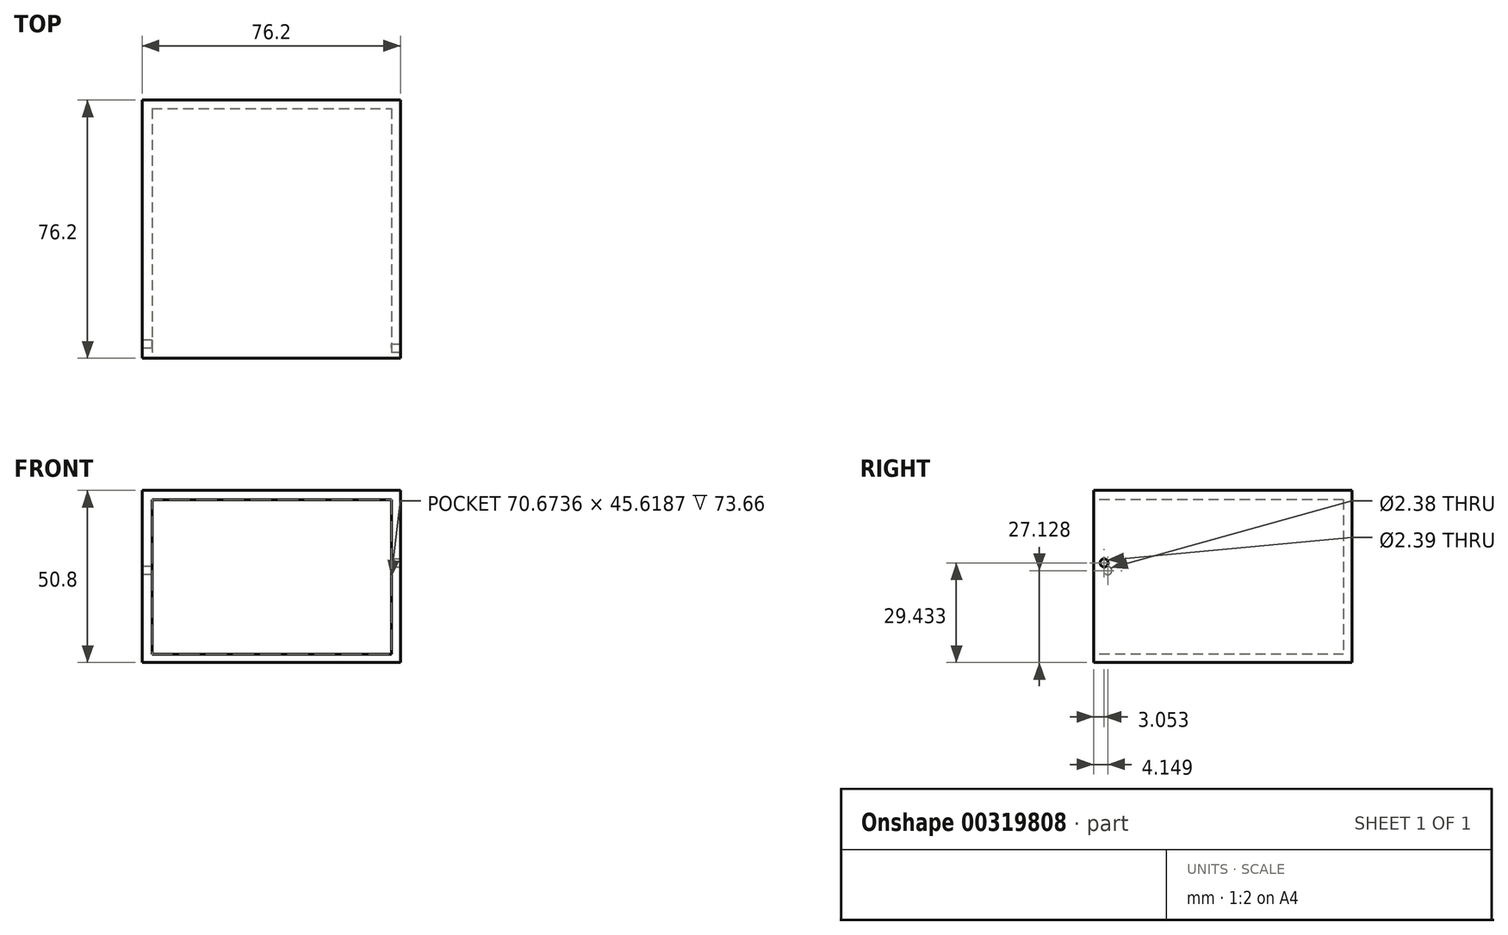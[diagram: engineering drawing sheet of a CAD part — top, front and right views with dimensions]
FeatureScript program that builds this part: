
annotation { "Feature Type Name" : "Feature", "Feature Type Description" : "" }
export const myFeature = defineFeature(function(context is Context, id is Id, definition is map)
    precondition{}
    {
        {
            var Q0;
            Q0=qCreatedBy(makeId("Front.planeOp"),FACE);
            var sketch = newSketch(context, id + "F0", { "sketchPlane" : qUnion([Q0])});
            skLineSegment(sketch, "E0.bottom", {"start": v(0, 0) * mm, "end": v(-76.2, 0) * mm});
            skLineSegment(sketch, "E0.top", {"start": v(0, 50.8) * mm, "end": v(-76.2, 50.8) * mm});
            skLineSegment(sketch, "E0.left", {"start": v(0, 0) * mm, "end": v(0, 50.8) * mm});
            skLineSegment(sketch, "E0.right", {"start": v(-76.2, 0) * mm, "end": v(-76.2, 50.8) * mm});
            skSolve(sketch);
        }
        {
            var Q0;
            Q0=makeQuery(id+"F0.imprint","IMPRINT",FACE,{"disambiguationData":[TD([[makeQuery(id+"F0.imprint","IMPRINT",EDGE,{"derivedFrom":sQuery(id+"F0.wireOp",EDGE,"E0.bottom")}),-1.0]])]});
            extrude(context, id + "F1", {"entities" : qUnion([Q0]), "depth" : 76.2 * mm});
        }
        {
            var Q0;
            Q0=makeQuery(id+"F1.opExtrude","CAP_FACE",FACE,{"disambiguationData":[OSD([sQuery(id+"F0.wireOp",EDGE,"E0.bottom"),sQuery(id+"F0.wireOp",EDGE,"E0.top"),sQuery(id+"F0.wireOp",EDGE,"E0.left"),sQuery(id+"F0.wireOp",EDGE,"E0.right")])],"isStart":false});
            var sketch = newSketch(context, id + "F2", { "sketchPlane" : qUnion([Q0])});
            skLineSegment(sketch, "E1.bottom", {"start": v(-73.27, 48.1) * mm, "end": v(-2.6, 48.1) * mm});
            skLineSegment(sketch, "E1.top", {"start": v(-73.27, 2.48) * mm, "end": v(-2.6, 2.48) * mm});
            skLineSegment(sketch, "E1.left", {"start": v(-73.27, 48.1) * mm, "end": v(-73.27, 2.48) * mm});
            skLineSegment(sketch, "E1.right", {"start": v(-2.6, 48.1) * mm, "end": v(-2.6, 2.48) * mm});
            skSolve(sketch);
        }
        {
            var Q0;
            Q0=makeQuery(id+"F2.imprint","IMPRINT",FACE,{"disambiguationData":[TD([[makeQuery(id+"F2.imprint","IMPRINT",EDGE,{"derivedFrom":sQuery(id+"F2.wireOp",EDGE,"E1.bottom")}),-1.0]])]});
            extrude(context, id + "F3", {"entities" : qUnion([Q0]), "operationType" : NewBodyOperationType.REMOVE, "oppositeDirection" : true, "depth" : 73.66 * mm});
        }
        {
            var Q0;
            Q0=makeQuery(id+"F1.opExtrude","SWEPT_FACE",FACE,{"disambiguationData":[OSD([sQuery(id+"F0.wireOp",EDGE,"E0.right")])]});
            var sketch = newSketch(context, id + "F4", { "sketchPlane" : qUnion([Q0])});
            skCircle(sketch, "E2", {"center": v(72.05, 27.13) * mm, "radius": 1.19 * mm});
            skSolve(sketch);
        }
        {
            var Q0;
            Q0=makeQuery(id+"F4.imprint","IMPRINT",FACE,{"disambiguationData":[TD([[makeQuery(id+"F4.imprint","IMPRINT",EDGE,{"derivedFrom":sQuery(id+"F4.wireOp",EDGE,"E2")}),1.0]])]});
            extrude(context, id + "F5", {"entities" : qUnion([Q0]), "operationType" : NewBodyOperationType.REMOVE, "oppositeDirection" : true, "depth" : 5.08 * mm});
        }
        {
            var Q0;
            Q0=makeQuery(id+"F1.opExtrude","SWEPT_FACE",FACE,{"disambiguationData":[OSD([sQuery(id+"F0.wireOp",EDGE,"E0.left")])]});
            var sketch = newSketch(context, id + "F6", { "sketchPlane" : qUnion([Q0])});
            skCircle(sketch, "E3", {"center": v(-73.15, 29.43) * mm, "radius": 1.2 * mm});
            skSolve(sketch);
        }
        {
            var Q0;
            Q0=makeQuery(id+"F6.imprint","IMPRINT",FACE,{"disambiguationData":[TD([[makeQuery(id+"F6.imprint","IMPRINT",EDGE,{"derivedFrom":sQuery(id+"F6.wireOp",EDGE,"E3")}),1.0]])]});
            extrude(context, id + "F7", {"entities" : qUnion([Q0]), "operationType" : NewBodyOperationType.REMOVE, "oppositeDirection" : true, "depth" : 5.08 * mm});
        }
    });
